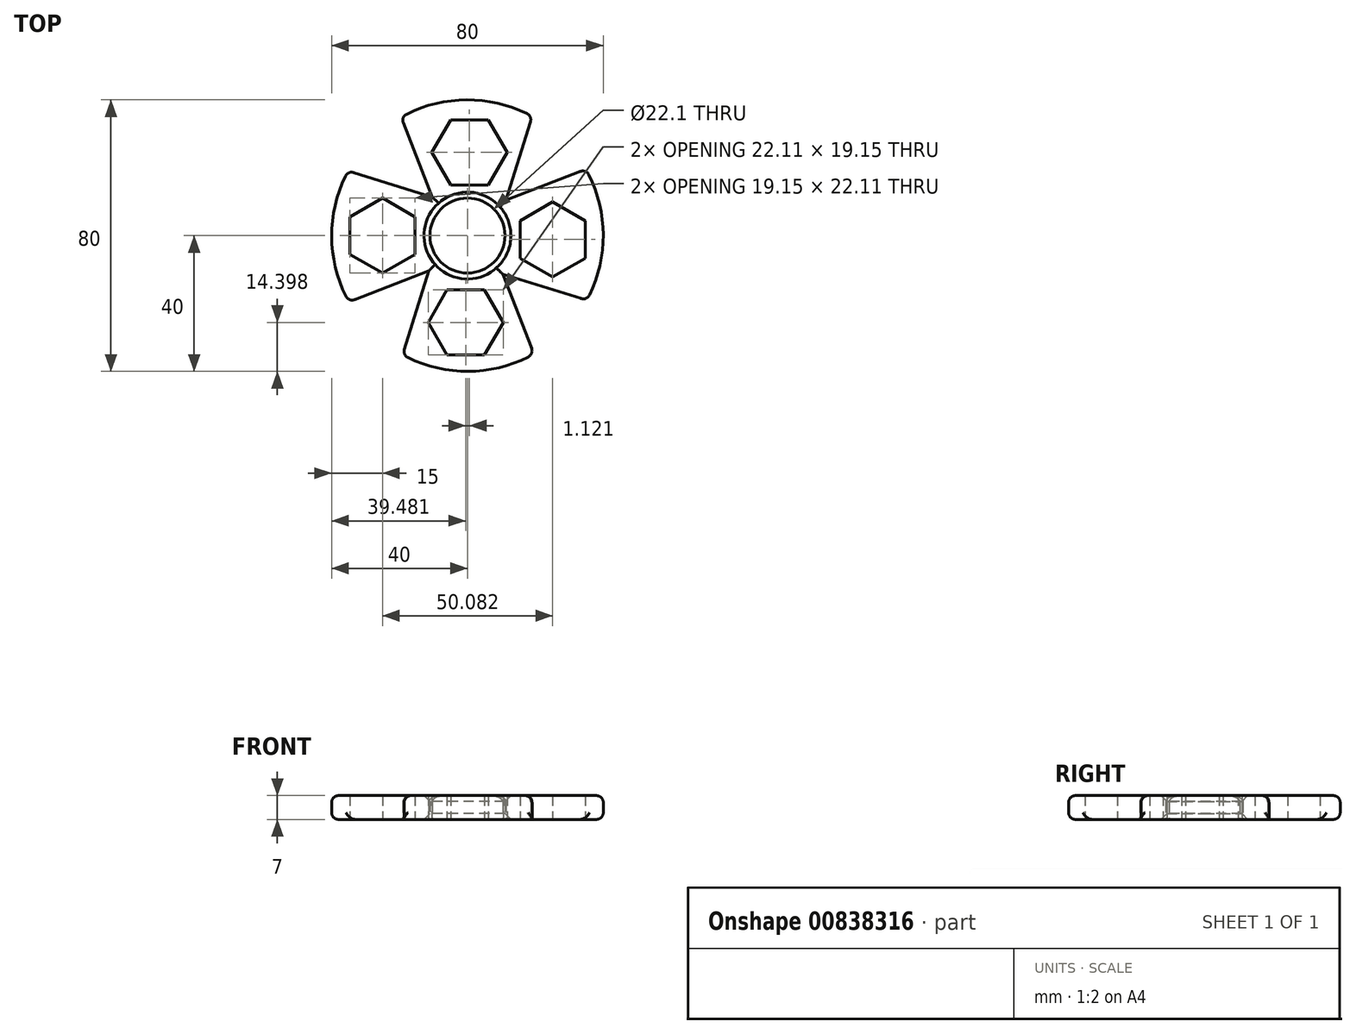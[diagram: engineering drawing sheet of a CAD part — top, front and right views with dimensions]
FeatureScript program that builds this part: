
annotation { "Feature Type Name" : "Feature", "Feature Type Description" : "" }
export const myFeature = defineFeature(function(context is Context, id is Id, definition is map)
    precondition{}
    {
        {
            var Q0;
            Q0=qCreatedBy(makeId("Top.planeOp"),FACE);
            var sketch = newSketch(context, id + "F0", { "sketchPlane" : qUnion([Q0])});
            skCircle(sketch, "E0", {"center": v(0, 0) * mm, "radius": 11.05 * mm});
            skCircle(sketch, "E1", {"center": v(0, 0) * mm, "radius": 40 * mm});
            skSolve(sketch);
        }
        {
            var Q0;
            Q0=makeQuery(id+"F0.imprint","IMPRINT",FACE,{"disambiguationData":[TD([[makeQuery(id+"F0.imprint","IMPRINT",EDGE,{"derivedFrom":sQuery(id+"F0.wireOp",EDGE,"E0")}),-1.0]])]});
            extrude(context, id + "F1", {"entities" : qUnion([Q0]), "depth" : 7 * mm, "offsetDistance" : 25 * mm});
        }
        {
            var Q0;
            Q0=qCreatedBy(makeId("Top.planeOp"),FACE);
            var sketch = newSketch(context, id + "F2", { "sketchPlane" : qUnion([Q0])});
            skCircle(sketch, "E2.cCircle", {"center": v(-25, 0) * mm, "radius": 9.58 * mm, "construction": true});
            skLineSegment(sketch, "E2.0", {"start": v(-15.42, -5.53) * mm, "end": v(-25, -11.06) * mm});
            skLineSegment(sketch, "E2.1", {"start": v(-25, -11.06) * mm, "end": v(-34.57, -5.53) * mm});
            skLineSegment(sketch, "E2.2", {"start": v(-34.57, -5.53) * mm, "end": v(-34.58, 5.53) * mm});
            skLineSegment(sketch, "E2.3", {"start": v(-34.58, 5.53) * mm, "end": v(-25, 11.06) * mm});
            skLineSegment(sketch, "E2.4", {"start": v(-25, 11.06) * mm, "end": v(-15.43, 5.53) * mm});
            skLineSegment(sketch, "E2.5", {"start": v(-15.43, 5.53) * mm, "end": v(-15.42, -5.53) * mm});
            skPoint(sketch, "E2.0.midPoint", {"position": v(-20.21, -8.3) * mm});
            skLineSegment(sketch, "E3.1.0", {"start": v(-11.58, -25.6) * mm, "end": v(-6.05, -16.03) * mm});
            skLineSegment(sketch, "E3.1.1", {"start": v(-6.05, -35.18) * mm, "end": v(-11.58, -25.6) * mm});
            skLineSegment(sketch, "E3.1.2", {"start": v(5, -35.18) * mm, "end": v(-6.05, -35.18) * mm});
            skLineSegment(sketch, "E3.1.3", {"start": v(10.54, -25.6) * mm, "end": v(5, -35.18) * mm});
            skLineSegment(sketch, "E3.1.4", {"start": v(5, -16.03) * mm, "end": v(10.54, -25.6) * mm});
            skLineSegment(sketch, "E3.1.5", {"start": v(-6.05, -16.03) * mm, "end": v(5, -16.03) * mm});
            skLineSegment(sketch, "E3.2.0", {"start": v(25.08, -12.18) * mm, "end": v(15.5, -6.65) * mm});
            skLineSegment(sketch, "E3.2.1", {"start": v(34.66, -6.65) * mm, "end": v(25.08, -12.18) * mm});
            skLineSegment(sketch, "E3.2.2", {"start": v(34.66, 4.4) * mm, "end": v(34.66, -6.65) * mm});
            skLineSegment(sketch, "E3.2.3", {"start": v(25.08, 9.94) * mm, "end": v(34.66, 4.4) * mm});
            skLineSegment(sketch, "E3.2.4", {"start": v(15.5, 4.4) * mm, "end": v(25.08, 9.94) * mm});
            skLineSegment(sketch, "E3.2.5", {"start": v(15.5, -6.65) * mm, "end": v(15.5, 4.4) * mm});
            skLineSegment(sketch, "E3.3.0", {"start": v(11.66, 24.48) * mm, "end": v(6.13, 14.9) * mm});
            skLineSegment(sketch, "E3.3.1", {"start": v(6.13, 34.06) * mm, "end": v(11.66, 24.48) * mm});
            skLineSegment(sketch, "E3.3.2", {"start": v(-4.93, 34.06) * mm, "end": v(6.13, 34.06) * mm});
            skLineSegment(sketch, "E3.3.3", {"start": v(-10.45, 24.48) * mm, "end": v(-4.93, 34.06) * mm});
            skLineSegment(sketch, "E3.3.4", {"start": v(-4.93, 14.9) * mm, "end": v(-10.45, 24.48) * mm});
            skLineSegment(sketch, "E3.3.5", {"start": v(6.13, 14.9) * mm, "end": v(-4.93, 14.9) * mm});
            skPoint(sketch, "E3.center", {"position": v(0.04, -0.56) * mm});
            skSolve(sketch);
        }
        {
            var Q0;
            Q0 = qSketchRegion(id + "F2", true);
            extrude(context, id + "F3", {"entities" : qUnion([Q0]), "operationType" : NewBodyOperationType.REMOVE, "endBound" : BoundingType.THROUGH_ALL, "depth" : 25 * mm, "offsetDistance" : 25 * mm});
        }
        {
            var Q0;
            Q0=qCreatedBy(makeId("Top.planeOp"),FACE);
            var sketch = newSketch(context, id + "F4", { "sketchPlane" : qUnion([Q0])});
            skLineSegment(sketch, "E4", {"start": v(-19.58, 35.02) * mm, "end": v(-10.44, 11.39) * mm});
            skLineSegment(sketch, "E5", {"start": v(-10.44, 11.39) * mm, "end": v(-58.22, 26.22) * mm});
            skLineSegment(sketch, "E6", {"start": v(-58.22, 26.22) * mm, "end": v(-19.58, 35.02) * mm});
            skLineSegment(sketch, "E7.1.0", {"start": v(-26.22, -58.22) * mm, "end": v(-35.02, -19.58) * mm});
            skLineSegment(sketch, "E7.1.1", {"start": v(-11.39, -10.44) * mm, "end": v(-26.22, -58.22) * mm});
            skLineSegment(sketch, "E7.1.2", {"start": v(-35.02, -19.58) * mm, "end": v(-11.39, -10.44) * mm});
            skLineSegment(sketch, "E7.2.0", {"start": v(58.22, -26.22) * mm, "end": v(19.58, -35.02) * mm});
            skLineSegment(sketch, "E7.2.1", {"start": v(10.44, -11.39) * mm, "end": v(58.22, -26.22) * mm});
            skLineSegment(sketch, "E7.2.2", {"start": v(19.58, -35.02) * mm, "end": v(10.44, -11.39) * mm});
            skLineSegment(sketch, "E7.3.0", {"start": v(26.22, 58.22) * mm, "end": v(35.02, 19.58) * mm});
            skLineSegment(sketch, "E7.3.1", {"start": v(11.39, 10.44) * mm, "end": v(26.22, 58.22) * mm});
            skLineSegment(sketch, "E7.3.2", {"start": v(35.02, 19.58) * mm, "end": v(11.39, 10.44) * mm});
            skPoint(sketch, "E7.center", {"position": v(0, 0) * mm});
            skSolve(sketch);
        }
        {
            var Q0;
            Q0=makeQuery(id+"F4.imprint","IMPRINT",FACE,{"disambiguationData":[TD([[makeQuery(id+"F4.imprint","IMPRINT",EDGE,{"derivedFrom":sQuery(id+"F4.wireOp",EDGE,"E4")}),-1.0]])]});
            var Q1;
            Q1=makeQuery(id+"F4.imprint","IMPRINT",FACE,{"disambiguationData":[TD([[makeQuery(id+"F4.imprint","IMPRINT",EDGE,{"derivedFrom":sQuery(id+"F4.wireOp",EDGE,"E7.1.0")}),-1.0]])]});
            var Q2;
            Q2=makeQuery(id+"F4.imprint","IMPRINT",FACE,{"disambiguationData":[TD([[makeQuery(id+"F4.imprint","IMPRINT",EDGE,{"derivedFrom":sQuery(id+"F4.wireOp",EDGE,"E7.2.0")}),-1.0]])]});
            var Q3;
            Q3=makeQuery(id+"F4.imprint","IMPRINT",FACE,{"disambiguationData":[TD([[makeQuery(id+"F4.imprint","IMPRINT",EDGE,{"derivedFrom":sQuery(id+"F4.wireOp",EDGE,"E7.3.0")}),-1.0]])]});
            extrude(context, id + "F5", {"entities" : qUnion([Q0, Q1, Q2, Q3]), "operationType" : NewBodyOperationType.REMOVE, "endBound" : BoundingType.THROUGH_ALL, "depth" : 25 * mm, "offsetDistance" : 25 * mm});
        }
        {
            var Q0;
            Q0=makeQuery(id+"F5.boolean.opBoolean","INTERSECT",EDGE,{"derivedFrom":[makeQuery(id+"F1.opExtrude","CAP_FACE",FACE,{"disambiguationData":[OSD([sQuery(id+"F0.wireOp",EDGE,"E0"),sQuery(id+"F0.wireOp",EDGE,"E1")])],"isStart":false}),makeQuery(id+"F5.opExtrude","SWEPT_FACE",FACE,{"disambiguationData":[OSD([sQuery(id+"F4.wireOp",EDGE,"E5")])]})]});
            var Q1;
            {var subQ0=sQuery(id+"F0.wireOp",EDGE,"E1");Q1=makeQuery(id+"F5.boolean.opBoolean","SPLIT",EDGE,{"disambiguationData":[TD([makeQuery(id+"F5.opExtrude","SWEPT_FACE",FACE,{"disambiguationData":[OSD([sQuery(id+"F4.wireOp",EDGE,"E5")])]})])],"derivedFrom":makeQuery(id+"F1.opExtrude","CAP_EDGE",EDGE,{"disambiguationData":[OSD([subQ0])],"isStart":false})});}
            var Q2;
            Q2=makeQuery(id+"F5.boolean.opBoolean","INTERSECT",EDGE,{"derivedFrom":[makeQuery(id+"F1.opExtrude","CAP_FACE",FACE,{"disambiguationData":[OSD([sQuery(id+"F0.wireOp",EDGE,"E0"),sQuery(id+"F0.wireOp",EDGE,"E1")])],"isStart":false}),makeQuery(id+"F5.opExtrude","SWEPT_FACE",FACE,{"disambiguationData":[OSD([sQuery(id+"F4.wireOp",EDGE,"E7.1.2")])]})]});
            var Q3;
            Q3=makeQuery(id+"F5.boolean.opBoolean","INTERSECT",EDGE,{"derivedFrom":[makeQuery(id+"F1.opExtrude","CAP_FACE",FACE,{"disambiguationData":[OSD([sQuery(id+"F0.wireOp",EDGE,"E0"),sQuery(id+"F0.wireOp",EDGE,"E1")])],"isStart":false}),makeQuery(id+"F5.opExtrude","SWEPT_FACE",FACE,{"disambiguationData":[OSD([sQuery(id+"F4.wireOp",EDGE,"E7.1.1")])]})]});
            var Q4;
            Q4=makeQuery(id+"F5.boolean.opBoolean","INTERSECT",EDGE,{"derivedFrom":[makeQuery(id+"F1.opExtrude","CAP_FACE",FACE,{"disambiguationData":[OSD([sQuery(id+"F0.wireOp",EDGE,"E0"),sQuery(id+"F0.wireOp",EDGE,"E1")])],"isStart":false}),makeQuery(id+"F5.opExtrude","SWEPT_FACE",FACE,{"disambiguationData":[OSD([sQuery(id+"F4.wireOp",EDGE,"E7.2.2")])]})]});
            var Q5;
            Q5=makeQuery(id+"F5.boolean.opBoolean","INTERSECT",EDGE,{"derivedFrom":[makeQuery(id+"F1.opExtrude","CAP_FACE",FACE,{"disambiguationData":[OSD([sQuery(id+"F0.wireOp",EDGE,"E0"),sQuery(id+"F0.wireOp",EDGE,"E1")])],"isStart":false}),makeQuery(id+"F5.opExtrude","SWEPT_FACE",FACE,{"disambiguationData":[OSD([sQuery(id+"F4.wireOp",EDGE,"E7.2.1")])]})]});
            var Q6;
            Q6=makeQuery(id+"F5.boolean.opBoolean","INTERSECT",EDGE,{"derivedFrom":[makeQuery(id+"F1.opExtrude","CAP_FACE",FACE,{"disambiguationData":[OSD([sQuery(id+"F0.wireOp",EDGE,"E0"),sQuery(id+"F0.wireOp",EDGE,"E1")])],"isStart":false}),makeQuery(id+"F5.opExtrude","SWEPT_FACE",FACE,{"disambiguationData":[OSD([sQuery(id+"F4.wireOp",EDGE,"E7.3.2")])]})]});
            var Q7;
            {var subQ0=sQuery(id+"F0.wireOp",EDGE,"E1");Q7=makeQuery(id+"F5.boolean.opBoolean","SPLIT",EDGE,{"disambiguationData":[TD([makeQuery(id+"F5.opExtrude","SWEPT_FACE",FACE,{"disambiguationData":[OSD([sQuery(id+"F4.wireOp",EDGE,"E7.2.1")])]})])],"derivedFrom":makeQuery(id+"F1.opExtrude","CAP_EDGE",EDGE,{"disambiguationData":[OSD([subQ0])],"isStart":false})});}
            var Q8;
            Q8=makeQuery(id+"F5.boolean.opBoolean","INTERSECT",EDGE,{"derivedFrom":[makeQuery(id+"F1.opExtrude","CAP_FACE",FACE,{"disambiguationData":[OSD([sQuery(id+"F0.wireOp",EDGE,"E0"),sQuery(id+"F0.wireOp",EDGE,"E1")])],"isStart":false}),makeQuery(id+"F5.opExtrude","SWEPT_FACE",FACE,{"disambiguationData":[OSD([sQuery(id+"F4.wireOp",EDGE,"E7.3.1")])]})]});
            var Q9;
            {var subQ0=sQuery(id+"F0.wireOp",EDGE,"E1");Q9=makeQuery(id+"F5.boolean.opBoolean","SPLIT",EDGE,{"disambiguationData":[TD([makeQuery(id+"F5.opExtrude","SWEPT_FACE",FACE,{"disambiguationData":[OSD([sQuery(id+"F4.wireOp",EDGE,"E4")])]})])],"derivedFrom":makeQuery(id+"F1.opExtrude","CAP_EDGE",EDGE,{"disambiguationData":[OSD([subQ0])],"isStart":false})});}
            var Q10;
            Q10=makeQuery(id+"F5.boolean.opBoolean","INTERSECT",EDGE,{"derivedFrom":[makeQuery(id+"F1.opExtrude","CAP_FACE",FACE,{"disambiguationData":[OSD([sQuery(id+"F0.wireOp",EDGE,"E0"),sQuery(id+"F0.wireOp",EDGE,"E1")])],"isStart":false}),makeQuery(id+"F5.opExtrude","SWEPT_FACE",FACE,{"disambiguationData":[OSD([sQuery(id+"F4.wireOp",EDGE,"E4")])]})]});
            var Q11;
            {var subQ0=sQuery(id+"F0.wireOp",EDGE,"E1");Q11=makeQuery(id+"F5.boolean.opBoolean","SPLIT",EDGE,{"disambiguationData":[TD([makeQuery(id+"F5.opExtrude","SWEPT_FACE",FACE,{"disambiguationData":[OSD([sQuery(id+"F4.wireOp",EDGE,"E5")])]})])],"derivedFrom":makeQuery(id+"F1.opExtrude","CAP_EDGE",EDGE,{"disambiguationData":[OSD([subQ0])],"isStart":true})});}
            var Q12;
            Q12=makeQuery(id+"F5.boolean.opBoolean","COPY",EDGE,{"derivedFrom":makeQuery(id+"F5.opExtrude","CAP_EDGE",EDGE,{"disambiguationData":[OSD([sQuery(id+"F4.wireOp",EDGE,"E5")])],"isStart":true})});
            var Q13;
            Q13=makeQuery(id+"F5.boolean.opBoolean","COPY",EDGE,{"derivedFrom":makeQuery(id+"F5.opExtrude","CAP_EDGE",EDGE,{"disambiguationData":[OSD([sQuery(id+"F4.wireOp",EDGE,"E4")])],"isStart":true})});
            var Q14;
            {var subQ0=sQuery(id+"F0.wireOp",EDGE,"E1");Q14=makeQuery(id+"F5.boolean.opBoolean","SPLIT",EDGE,{"disambiguationData":[TD([makeQuery(id+"F5.opExtrude","SWEPT_FACE",FACE,{"disambiguationData":[OSD([sQuery(id+"F4.wireOp",EDGE,"E4")])]})])],"derivedFrom":makeQuery(id+"F1.opExtrude","CAP_EDGE",EDGE,{"disambiguationData":[OSD([subQ0])],"isStart":true})});}
            var Q15;
            Q15=makeQuery(id+"F5.boolean.opBoolean","COPY",EDGE,{"derivedFrom":makeQuery(id+"F5.opExtrude","CAP_EDGE",EDGE,{"disambiguationData":[OSD([sQuery(id+"F4.wireOp",EDGE,"E7.3.1")])],"isStart":true})});
            var Q16;
            Q16=makeQuery(id+"F5.boolean.opBoolean","COPY",EDGE,{"derivedFrom":makeQuery(id+"F5.opExtrude","CAP_EDGE",EDGE,{"disambiguationData":[OSD([sQuery(id+"F4.wireOp",EDGE,"E7.3.2")])],"isStart":true})});
            var Q17;
            {var subQ0=sQuery(id+"F0.wireOp",EDGE,"E1");Q17=makeQuery(id+"F5.boolean.opBoolean","SPLIT",EDGE,{"disambiguationData":[TD([makeQuery(id+"F5.opExtrude","SWEPT_FACE",FACE,{"disambiguationData":[OSD([sQuery(id+"F4.wireOp",EDGE,"E7.2.1")])]})])],"derivedFrom":makeQuery(id+"F1.opExtrude","CAP_EDGE",EDGE,{"disambiguationData":[OSD([subQ0])],"isStart":true})});}
            var Q18;
            Q18=makeQuery(id+"F5.boolean.opBoolean","COPY",EDGE,{"derivedFrom":makeQuery(id+"F5.opExtrude","CAP_EDGE",EDGE,{"disambiguationData":[OSD([sQuery(id+"F4.wireOp",EDGE,"E7.2.1")])],"isStart":true})});
            var Q19;
            Q19=makeQuery(id+"F5.boolean.opBoolean","COPY",EDGE,{"derivedFrom":makeQuery(id+"F5.opExtrude","CAP_EDGE",EDGE,{"disambiguationData":[OSD([sQuery(id+"F4.wireOp",EDGE,"E7.2.2")])],"isStart":true})});
            var Q20;
            {var subQ0=sQuery(id+"F0.wireOp",EDGE,"E1");Q20=makeQuery(id+"F5.boolean.opBoolean","SPLIT",EDGE,{"disambiguationData":[TD([makeQuery(id+"F5.opExtrude","SWEPT_FACE",FACE,{"disambiguationData":[OSD([sQuery(id+"F4.wireOp",EDGE,"E7.1.1")])]})])],"derivedFrom":makeQuery(id+"F1.opExtrude","CAP_EDGE",EDGE,{"disambiguationData":[OSD([subQ0])],"isStart":true})});}
            var Q21;
            Q21=makeQuery(id+"F5.boolean.opBoolean","COPY",EDGE,{"derivedFrom":makeQuery(id+"F5.opExtrude","CAP_EDGE",EDGE,{"disambiguationData":[OSD([sQuery(id+"F4.wireOp",EDGE,"E7.1.1")])],"isStart":true})});
            var Q22;
            Q22=makeQuery(id+"F5.boolean.opBoolean","COPY",EDGE,{"derivedFrom":makeQuery(id+"F5.opExtrude","CAP_EDGE",EDGE,{"disambiguationData":[OSD([sQuery(id+"F4.wireOp",EDGE,"E7.1.2")])],"isStart":true})});
            var Q23;
            {var subQ0=sQuery(id+"F0.wireOp",EDGE,"E1");Q23=makeQuery(id+"F5.boolean.opBoolean","SPLIT",EDGE,{"disambiguationData":[TD([makeQuery(id+"F5.opExtrude","SWEPT_FACE",FACE,{"disambiguationData":[OSD([sQuery(id+"F4.wireOp",EDGE,"E7.1.1")])]})])],"derivedFrom":makeQuery(id+"F1.opExtrude","CAP_EDGE",EDGE,{"disambiguationData":[OSD([subQ0])],"isStart":false})});}
            var Q24;
            Q24=makeQuery(id+"F5.boolean.opBoolean","INTERSECT",EDGE,{"derivedFrom":[makeQuery(id+"F1.opExtrude","SWEPT_FACE",FACE,{"disambiguationData":[OSD([sQuery(id+"F0.wireOp",EDGE,"E1")])]}),makeQuery(id+"F5.opExtrude","SWEPT_FACE",FACE,{"disambiguationData":[OSD([sQuery(id+"F4.wireOp",EDGE,"E7.2.2")])]})]});
            var Q25;
            Q25=makeQuery(id+"F5.boolean.opBoolean","INTERSECT",EDGE,{"derivedFrom":[makeQuery(id+"F1.opExtrude","SWEPT_FACE",FACE,{"disambiguationData":[OSD([sQuery(id+"F0.wireOp",EDGE,"E1")])]}),makeQuery(id+"F5.opExtrude","SWEPT_FACE",FACE,{"disambiguationData":[OSD([sQuery(id+"F4.wireOp",EDGE,"E7.1.1")])]})]});
            var Q26;
            Q26=makeQuery(id+"F5.boolean.opBoolean","INTERSECT",EDGE,{"derivedFrom":[makeQuery(id+"F1.opExtrude","SWEPT_FACE",FACE,{"disambiguationData":[OSD([sQuery(id+"F0.wireOp",EDGE,"E1")])]}),makeQuery(id+"F5.opExtrude","SWEPT_FACE",FACE,{"disambiguationData":[OSD([sQuery(id+"F4.wireOp",EDGE,"E7.1.2")])]})]});
            var Q27;
            Q27=makeQuery(id+"F5.boolean.opBoolean","INTERSECT",EDGE,{"derivedFrom":[makeQuery(id+"F1.opExtrude","SWEPT_FACE",FACE,{"disambiguationData":[OSD([sQuery(id+"F0.wireOp",EDGE,"E1")])]}),makeQuery(id+"F5.opExtrude","SWEPT_FACE",FACE,{"disambiguationData":[OSD([sQuery(id+"F4.wireOp",EDGE,"E5")])]})]});
            var Q28;
            Q28=makeQuery(id+"F5.boolean.opBoolean","INTERSECT",EDGE,{"derivedFrom":[makeQuery(id+"F1.opExtrude","SWEPT_FACE",FACE,{"disambiguationData":[OSD([sQuery(id+"F0.wireOp",EDGE,"E1")])]}),makeQuery(id+"F5.opExtrude","SWEPT_FACE",FACE,{"disambiguationData":[OSD([sQuery(id+"F4.wireOp",EDGE,"E4")])]})]});
            var Q29;
            Q29=makeQuery(id+"F5.boolean.opBoolean","INTERSECT",EDGE,{"derivedFrom":[makeQuery(id+"F1.opExtrude","SWEPT_FACE",FACE,{"disambiguationData":[OSD([sQuery(id+"F0.wireOp",EDGE,"E1")])]}),makeQuery(id+"F5.opExtrude","SWEPT_FACE",FACE,{"disambiguationData":[OSD([sQuery(id+"F4.wireOp",EDGE,"E7.3.1")])]})]});
            var Q30;
            Q30=makeQuery(id+"F5.boolean.opBoolean","INTERSECT",EDGE,{"derivedFrom":[makeQuery(id+"F1.opExtrude","SWEPT_FACE",FACE,{"disambiguationData":[OSD([sQuery(id+"F0.wireOp",EDGE,"E1")])]}),makeQuery(id+"F5.opExtrude","SWEPT_FACE",FACE,{"disambiguationData":[OSD([sQuery(id+"F4.wireOp",EDGE,"E7.3.2")])]})]});
            var Q31;
            Q31=makeQuery(id+"F5.boolean.opBoolean","INTERSECT",EDGE,{"derivedFrom":[makeQuery(id+"F1.opExtrude","SWEPT_FACE",FACE,{"disambiguationData":[OSD([sQuery(id+"F0.wireOp",EDGE,"E1")])]}),makeQuery(id+"F5.opExtrude","SWEPT_FACE",FACE,{"disambiguationData":[OSD([sQuery(id+"F4.wireOp",EDGE,"E7.2.1")])]})]});
            fillet(context, id + "F6", {"entities" : qUnion([Q0, Q1, Q2, Q3, Q4, Q5, Q6, Q7, Q8, Q9, Q10, Q11, Q12, Q13, Q14, Q15, Q16, Q17, Q18, Q19, Q20, Q21, Q22, Q23, Q24, Q25, Q26, Q27, Q28, Q29, Q30, Q31]), "radius" : 2 * mm, "tangentPropagation" : true, "allowEdgeOverflow" : false});
        }
        {
            var Q0;
            Q0=makeQuery(id+"F1.opExtrude","CAP_EDGE",EDGE,{"disambiguationData":[OSD([sQuery(id+"F0.wireOp",EDGE,"E0")])],"isStart":false});
            var Q1;
            Q1=makeQuery(id+"F1.opExtrude","CAP_EDGE",EDGE,{"disambiguationData":[OSD([sQuery(id+"F0.wireOp",EDGE,"E0")])],"isStart":true});
            chamfer(context, id + "F7", {"entities" : qUnion([Q0, Q1]), "width" : 1.75 * mm, "tangentPropagation" : true});
        }
    });
